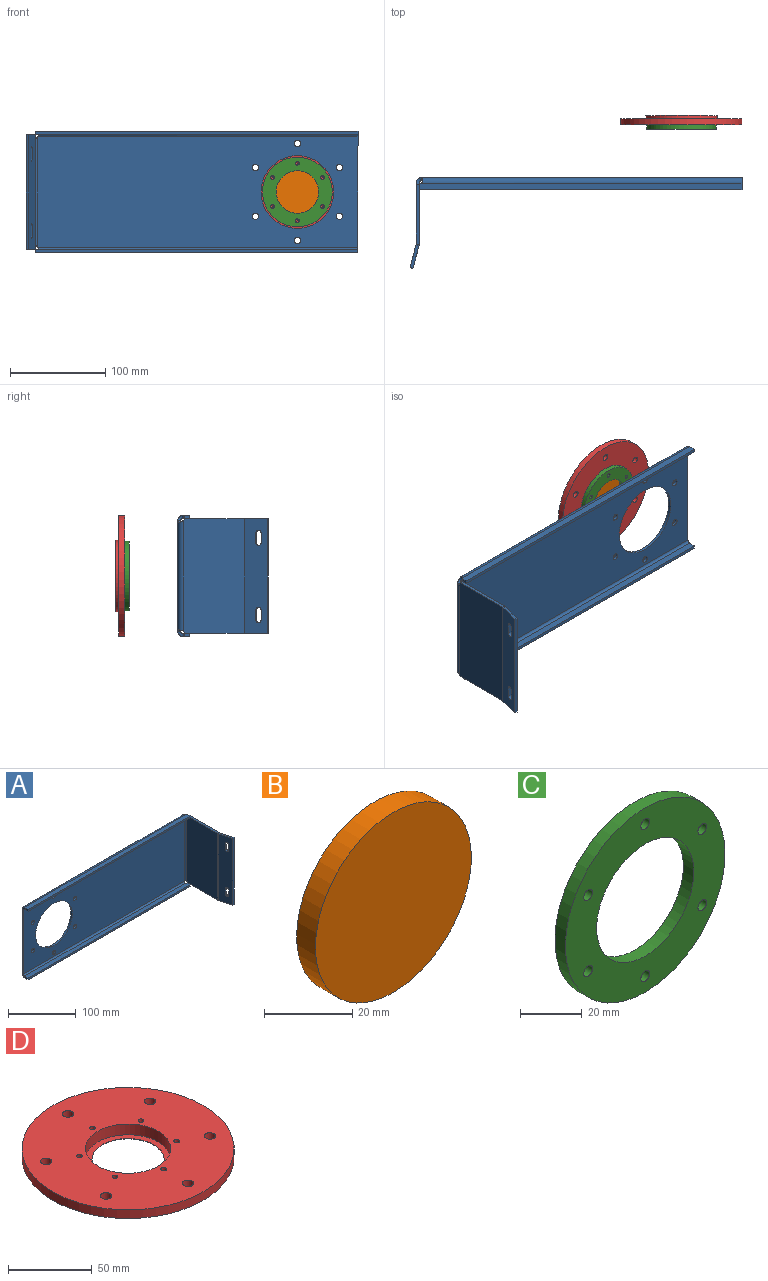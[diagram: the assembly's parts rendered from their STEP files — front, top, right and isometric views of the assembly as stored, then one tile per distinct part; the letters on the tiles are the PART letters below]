
ASSEMBLY  parts=4 mates=7
PART A: 57 faces, bbox 347.8x95.1x127 mm
  f0: plane 5.77x3.18mm, normal (1,0,0), area 18.3mm2, adj f1,f2,f4,f5
  f1: plane 337.9x6.99mm, normal (0,0,-1), area 2358.5mm2, adj f0,f2,f3,f5,f55
  f2: plane 337.9x3.18mm, normal (0,-1,0), area 1072.8mm2, adj f0,f1,f3,f4
  f3: plane 6.99x3.18mm, normal (-1,0,0), area 22.2mm2, adj f1,f2,f4,f53
  f4: plane 337.9x6.99mm, normal (0,0,1), area 2358.5mm2, adj f0,f2,f3,f5,f56
  f5: cylinder r=4.41mm len=3.18mm, axis (0,0,1), area 8.3mm2, adj f0,f1,f4,f54
  f6: cylinder r=3.38mm len=6.76mm, axis (0,-1,0), area 67.4mm2, adj f14,f15
  f7: cylinder r=3.38mm len=6.76mm, axis (0,-1,0), area 67.4mm2, adj f14,f15
  f8: cylinder r=3.38mm len=6.76mm, axis (0,-1,0), area 67.4mm2, adj f14,f15
  f9: cylinder r=3.38mm len=6.76mm, axis (0,-1,0), area 67.4mm2, adj f14,f15
  f10: cylinder r=3.38mm len=6.76mm, axis (0,-1,0), area 67.4mm2, adj f14,f15
  f11: cylinder r=3.38mm len=6.76mm, axis (0,-1,0), area 67.4mm2, adj f14,f15
  f12: cylinder r=38.1mm len=76.2mm, axis (0,-1,0), area 760.1mm2, adj f14,f15
  f13: plane 115.57x3.18mm, normal (-1,0,0), area 366.9mm2, adj f14,f15,f22,f53
  f14: plane 335.61x115.57mm, normal (0,1,0), area 34011mm2, adj f6,f7,f8,f9,f10,f11,f12,f13
  f15: plane 335.61x115.57mm, normal (0,-1,0), area 34011mm2, adj f6,f7,f8,f9,f10,f11,f12,f13
  f16: plane 5.77x3.18mm, normal (1,0,0), area 18.3mm2, adj f18,f19,f20,f21
  f17: plane 6.99x3.18mm, normal (-1,0,0), area 22.2mm2, adj f18,f19,f20,f22
  f18: plane 337.9x3.18mm, normal (0,-1,0), area 1072.8mm2, adj f16,f17,f19,f20
  f19: plane 337.9x6.99mm, normal (0,0,1), area 2358.5mm2, adj f16,f17,f18,f21,f24
  f20: plane 337.9x6.99mm, normal (0,0,-1), area 2358.5mm2, adj f16,f17,f18,f21,f25
  f21: cylinder r=4.41mm len=3.18mm, axis (0,0,-1), area 8.3mm2, adj f16,f19,f20,f23
  f22: plane 5.72x5.72mm, normal (-1,0,0), area 20.6mm2, adj f13,f17,f24,f25
  f23: bspline ~5.72x5.72mm, area 22.8mm2, adj f21,f24,f25,f49
  f24: cylinder r=5.71mm len=335.61mm, axis (-1,0,0), area 3004.8mm2, adj f14,f19,f22,f23
  f25: cylinder r=2.54mm len=335.61mm, axis (-1,0,0), area 1335.5mm2, adj f15,f20,f22,f23
  f26: plane 62.84x3.18mm, normal (0,0,-1), area 199.5mm2, adj f28,f29,f30,f45
  f27: plane 62.84x3.18mm, normal (0,0,1), area 199.5mm2, adj f28,f29,f31,f46
  f28: plane 120.14x64.05mm, normal (1,0,0), area 7692.2mm2, adj f26,f27,f30,f31,f48,f51
  f29: plane 120.14x64.05mm, normal (-1,0,0), area 7692.2mm2, adj f26,f27,f30,f31,f47,f52
  f30: cylinder r=4.41mm len=3.18mm, axis (-1,0,0), area 8.3mm2, adj f26,f28,f29,f50
  f31: cylinder r=4.41mm len=3.18mm, axis (-1,0,0), area 8.3mm2, adj f27,f28,f29,f49
  f32: cylinder r=2.92mm len=6.46mm, axis (0.97,0.26,0), area 29.1mm2, adj f33,f42,f43,f44
  f33: plane 10.03x3.07mm, normal (0.26,-0.97,0), area 31.9mm2, adj f32,f34,f43,f44
  f34: cylinder r=2.92mm len=6.46mm, axis (0.97,0.26,0), area 29.1mm2, adj f33,f42,f43,f44
  f35: cylinder r=2.92mm len=6.46mm, axis (0.97,0.26,0), area 29.1mm2, adj f36,f41,f43,f44
  f36: plane 10.03x3.07mm, normal (0.26,-0.97,0), area 31.9mm2, adj f35,f37,f43,f44
  f37: cylinder r=2.92mm len=6.46mm, axis (0.97,0.26,0), area 29.1mm2, adj f36,f41,f43,f44
  f38: plane 120.14x3.07mm, normal (0.26,-0.97,0), area 381.5mm2, adj f39,f40,f43,f44
  f39: plane 24.63x9.45mm, normal (0,0,-1), area 78.3mm2, adj f38,f43,f44,f45
  f40: plane 24.63x9.45mm, normal (0,0,1), area 78.3mm2, adj f38,f43,f44,f46
  f41: plane 10.03x3.07mm, normal (-0.26,0.97,0), area 31.9mm2, adj f35,f37,f43,f44
  f42: plane 10.03x3.07mm, normal (-0.26,0.97,0), area 31.9mm2, adj f32,f34,f43,f44
  f43: plane 120.14x23.81mm, normal (0.97,0.26,0), area 2790.4mm2, adj f32,f33,f34,f35,f36,f37,f38,f39
  f44: plane 120.14x23.81mm, normal (-0.97,-0.26,0), area 2790.4mm2, adj f32,f33,f34,f35,f36,f37,f38,f39
  f45: plane 3.26x1.48mm, normal (0,0,-1), area 3.4mm2, adj f26,f39,f47,f48
  f46: plane 3.26x1.48mm, normal (0,0,1), area 3.4mm2, adj f27,f40,f47,f48
  f47: cylinder r=5.71mm len=120.14mm, axis (0,0,-1), area 179.8mm2, adj f29,f44,f45,f46
  f48: cylinder r=2.54mm len=120.14mm, axis (0,0,-1), area 79.9mm2, adj f28,f43,f45,f46
  f49: bspline ~5.72x5.72mm, area 22.8mm2, adj f23,f31,f51,f52
  f50: bspline ~5.72x5.72mm, area 22.8mm2, adj f30,f51,f52,f54
  f51: cylinder r=5.71mm len=115.57mm, axis (0,0,1), area 1021.5mm2, adj f14,f28,f49,f50
  f52: cylinder r=2.54mm len=115.57mm, axis (0,0,1), area 454mm2, adj f15,f29,f49,f50
  f53: plane 5.72x5.72mm, normal (-1,0,0), area 20.6mm2, adj f3,f13,f55,f56
  f54: bspline ~5.72x5.72mm, area 22.8mm2, adj f5,f50,f55,f56
  f55: cylinder r=5.71mm len=335.61mm, axis (-1,0,0), area 3004.8mm2, adj f1,f14,f53,f54
  f56: cylinder r=2.54mm len=335.61mm, axis (-1,0,0), area 1335.5mm2, adj f4,f15,f53,f54
PART B: 3 faces, bbox 50x6x50 mm
  f0: cylinder r=25mm len=50mm, axis (0,1,0), area 942.5mm2, adj f1,f2
  f1: plane 50x50mm, normal (0,-1,0), area 1963.5mm2, adj f0
  f2: plane 50x50mm, normal (0,1,0), area 1963.5mm2, adj f0
PART C: 10 faces, bbox 73x4.8x73 mm
  f0: cylinder r=36.51mm len=73.03mm, axis (0,1,0), area 1095.5mm2, adj f1,f2
  f1: plane 73.03x73.03mm, normal (0,-1,0), area 2561.1mm2, adj f0,f3,f4,f5,f6,f7,f8,f9
  f2: plane 73.03x73.03mm, normal (0,1,0), area 2561.1mm2, adj f0,f3,f4,f5,f6,f7,f8,f9
  f3: cylinder r=22.23mm len=44.45mm, axis (0,-1,0), area 666.8mm2, adj f1,f2
  f4: cylinder r=2mm len=4.78mm, axis (0,-1,0), area 60mm2, adj f1,f2
  f5: cylinder r=2mm len=4.78mm, axis (0,-1,0), area 60mm2, adj f1,f2
  f6: cylinder r=2mm len=4.78mm, axis (0,-1,0), area 60mm2, adj f1,f2
  f7: cylinder r=2mm len=4.78mm, axis (0,-1,0), area 60mm2, adj f1,f2
  f8: cylinder r=2mm len=4.78mm, axis (0,-1,0), area 60mm2, adj f1,f2
  f9: cylinder r=2mm len=4.78mm, axis (0,-1,0), area 60mm2, adj f1,f2
PART D: 27 faces, bbox 127x127x9.7 mm
  f0: plane 74.93x74.93mm, normal (0,0,-1), area 2072.1mm2, adj f1,f8
  f1: cylinder r=37.46mm len=74.93mm, axis (0,0,1), area 777.3mm2, adj f0,f2
  f2: plane 127x127mm, normal (0,0,-1), area 8042.9mm2, adj f1,f3,f21,f22,f23,f24,f25,f26
  f3: cylinder r=63.5mm len=127mm, axis (0,0,1), area 2533.5mm2, adj f2,f4
  f4: plane 127x127mm, normal (0,0,1), area 10349.2mm2, adj f3,f5,f10,f12,f14,f16,f18,f20
  f5: cylinder r=25.53mm len=51.05mm, axis (0,0,1), area 1262.9mm2, adj f4,f6
  f6: plane 51.05x51.05mm, normal (0,0,1), area 582.8mm2, adj f5,f7
  f7: cylinder r=21.59mm len=43.18mm, axis (0,0,1), area 34.5mm2, adj f6,f8
  f8: cone r=21.59mm half-angle=75deg, axis (0,0,-1), area 904mm2, adj f0,f7
  f9: cone r=0mm half-angle=59deg, axis (0,0,1), area 10.9mm2, adj f10
  f10: cylinder r=1.73mm len=5.56mm, axis (0,0,1), area 60.3mm2, adj f4,f9
  f11: cone r=0mm half-angle=59deg, axis (0,0,1), area 10.9mm2, adj f12
  f12: cylinder r=1.73mm len=5.56mm, axis (0,0,1), area 60.3mm2, adj f4,f11
  f13: cone r=0mm half-angle=59deg, axis (0,0,1), area 10.9mm2, adj f14
  f14: cylinder r=1.73mm len=5.56mm, axis (0,0,1), area 60.3mm2, adj f4,f13
  f15: cone r=0mm half-angle=59deg, axis (0,0,1), area 10.9mm2, adj f16
  f16: cylinder r=1.73mm len=5.56mm, axis (0,0,1), area 60.3mm2, adj f4,f15
  f17: cone r=0mm half-angle=59deg, axis (0,0,1), area 10.9mm2, adj f18
  f18: cylinder r=1.73mm len=5.56mm, axis (0,0,1), area 60.3mm2, adj f4,f17
  f19: cone r=0mm half-angle=59deg, axis (0,0,1), area 10.9mm2, adj f20
  f20: cylinder r=1.73mm len=5.56mm, axis (0,0,1), area 60.3mm2, adj f4,f19
  f21: cylinder r=3.38mm len=6.76mm, axis (0,0,-1), area 134.8mm2, adj f2,f4
  f22: cylinder r=3.38mm len=6.76mm, axis (0,0,-1), area 134.8mm2, adj f2,f4
  f23: cylinder r=3.38mm len=6.76mm, axis (0,0,-1), area 134.8mm2, adj f2,f4
  f24: cylinder r=3.38mm len=6.76mm, axis (0,0,-1), area 134.8mm2, adj f2,f4
  f25: cylinder r=3.38mm len=6.76mm, axis (0,0,-1), area 134.8mm2, adj f2,f4
  f26: cylinder r=3.38mm len=6.76mm, axis (0,0,-1), area 134.8mm2, adj f2,f4
PLACE A rot(axis=(0,-1,0),180deg) t=(-274.91,-59.46,59.63)mm
PLACE B rot(axis=(0,-1,0),92.3deg) t=(-0.26,7.03,-0.7)mm
PLACE C t=(-0.26,-0.84,-0.7)mm fixed
PLACE D rot(axis=(0.38,-0.65,0.65),138.6deg) t=(-0.26,8.81,-0.7)mm
MATE cylindrical D.f17 <-> C.f4  axis (0,-1,0) through (-26.38,1.94,14.38)mm
MATE planar D.f1 <-> C.f5  axis (0,-1,0) through (-0.26,-0.84,-0.7)mm
MATE cylindrical A.f7 <-> D.f25  axis (0,-1,0) through (43.74,-57.87,-26.1)mm
MATE cylindrical B.f0 <-> D.f1  axis (0,1,0) through (-0.26,4.03,-0.7)mm
MATE cylindrical D.f22 <-> A.f10  axis (0,1,0) through (-44.25,2.33,24.7)mm
MATE cylindrical D.f15 <-> C.f9  axis (0,-1,0) through (-0.26,1.94,29.46)mm
MATE planar D.f1 <-> B.f0  axis (0,-1,0) through (-0.26,7.03,-0.7)mm
